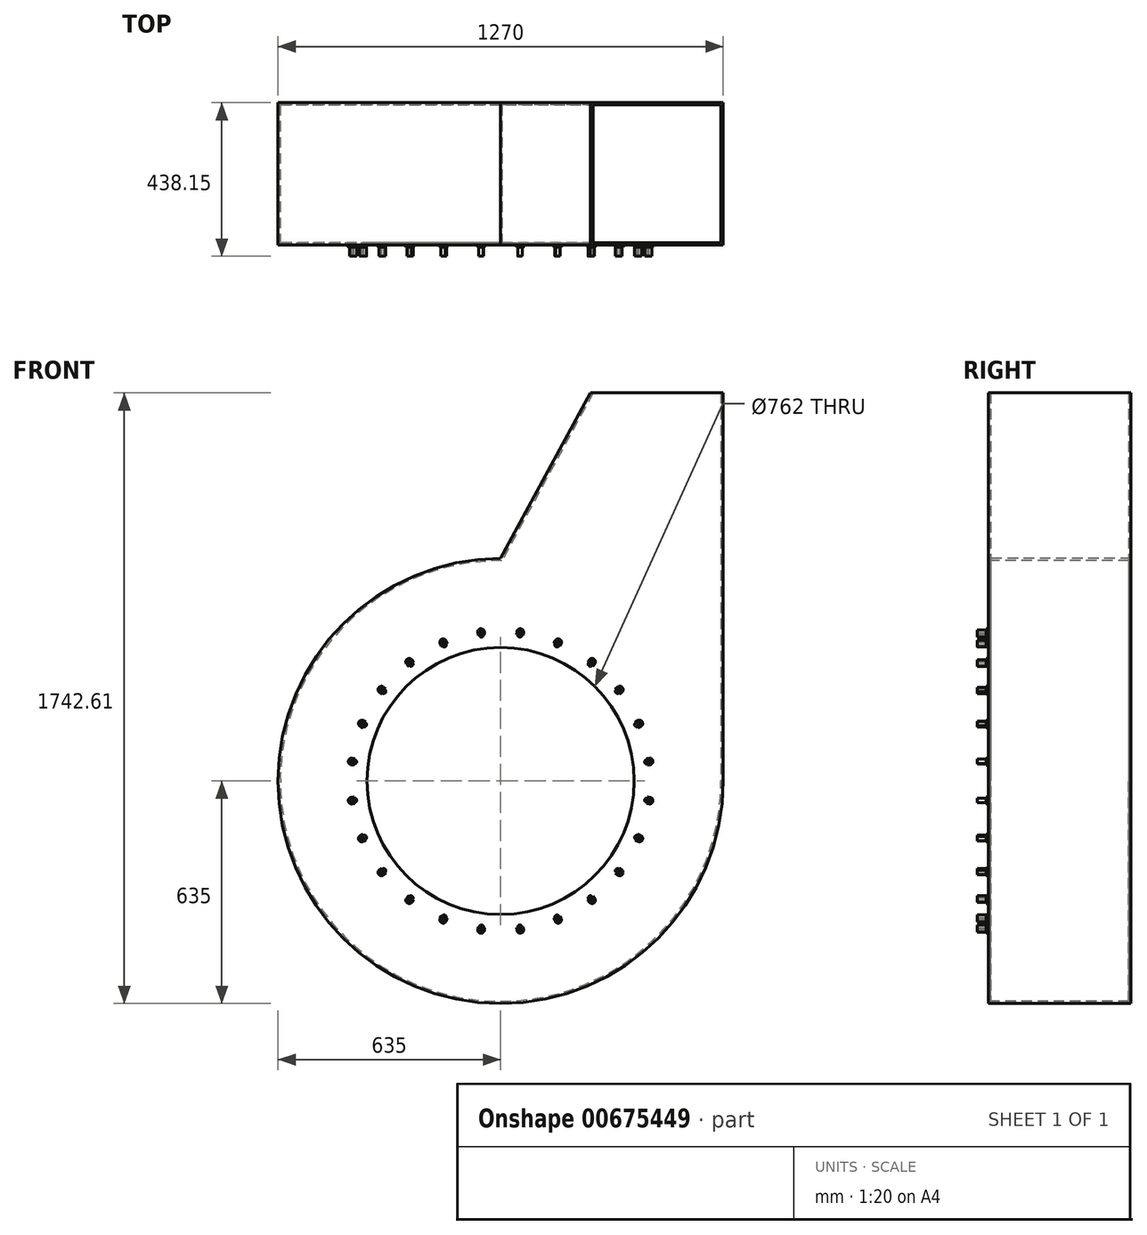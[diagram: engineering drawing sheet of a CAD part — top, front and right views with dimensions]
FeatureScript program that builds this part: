
annotation { "Feature Type Name" : "Feature", "Feature Type Description" : "" }
export const myFeature = defineFeature(function(context is Context, id is Id, definition is map)
    precondition{}
    {
        {
            var Q0;
            Q0=qCreatedBy(makeId("Front.planeOp"),FACE);
            var sketch = newSketch(context, id + "F0", { "sketchPlane" : qUnion([Q0])});
            skCircle(sketch, "E0", {"center": v(0, 0) * mm, "radius": 635 * mm});
            skLineSegment(sketch, "E1", {"start": v(635, 1107.6) * mm, "end": v(256.57, 1107.6) * mm});
            skLineSegment(sketch, "E2", {"start": v(256.57, 1107.6) * mm, "end": v(0, 635) * mm});
            skLineSegment(sketch, "E3", {"start": v(635, 1107.6) * mm, "end": v(635, 0) * mm});
            skCircle(sketch, "E4", {"center": v(0, 0) * mm, "radius": 428.63 * mm, "construction": true});
            skLineSegment(sketch, "E5", {"start": v(0, 0) * mm, "end": v(0, 611.06) * mm, "construction": true});
            skLineSegment(sketch, "E6", {"start": v(0, 0) * mm, "end": v(80.45, 611.06) * mm, "construction": true});
            skCircle(sketch, "E7", {"center": v(55.95, 424.96) * mm, "radius": 6.35 * mm});
            skCircle(sketch, "E8", {"center": v(0, 0) * mm, "radius": 381 * mm});
            skSolve(sketch);
        }
        {
            var Q0;
            Q0=qCreatedBy(makeId("Front.planeOp"),FACE);
            var sketch = newSketch(context, id + "F1", { "sketchPlane" : qUnion([Q0])});
            skCircle(sketch, "E9", {"center": v(0, 0) * mm, "radius": 420.69 * mm, "construction": true});
            skLineSegment(sketch, "E10.0", {"start": v(0, 0) * mm, "end": v(80.45, 611.06) * mm, "construction": true});
            skCircle(sketch, "E11", {"center": v(54.91, 417.09) * mm, "radius": 6.35 * mm});
            skSolve(sketch);
        }
        {
            var Q0;
            Q0=makeQuery(id+"F0.imprint","IMPRINT",FACE,{"disambiguationData":[TD([[makeQuery(id+"F0.imprint","IMPRINT",EDGE,{"derivedFrom":sQuery(id+"F0.wireOp",EDGE,"E1")}),1.0]])]});
            var Q1;
            Q1=makeQuery(id+"F0.imprint","IMPRINT",FACE,{"disambiguationData":[TD([[makeQuery(id+"F0.imprint","IMPRINT",EDGE,{"derivedFrom":sQuery(id+"F0.wireOp",EDGE,"E7")}),-1.0]])]});
            var Q2;
            Q2=makeQuery(id+"F0.imprint","IMPRINT",FACE,{"disambiguationData":[TD([[makeQuery(id+"F0.imprint","IMPRINT",EDGE,{"derivedFrom":sQuery(id+"F0.wireOp",EDGE,"E8")}),1.0]])]});
            var Q3;
            Q3=makeQuery(id+"F0.imprint","IMPRINT",FACE,{"disambiguationData":[TD([[makeQuery(id+"F0.imprint","IMPRINT",EDGE,{"derivedFrom":sQuery(id+"F0.wireOp",EDGE,"E7")}),1.0]])]});
            extrude(context, id + "F2", {"entities" : qUnion([Q0, Q1, Q2, Q3]), "oppositeDirection" : true, "depth" : 406.4 * mm, "offsetDistance" : 25.4 * mm});
        }
        {
            var Q0;
            Q0=makeQuery(id+"F2.opExtrude","SWEPT_FACE",FACE,{"disambiguationData":[OSD([sQuery(id+"F0.wireOp",EDGE,"E1")])]});
            shell(context, id + "F3", {"entities" : qUnion([Q0]), "thickness" : 6.35 * mm});
        }
        {
            var Q0;
            Q0=makeQuery(id+"F0.imprint","IMPRINT",FACE,{"disambiguationData":[TD([[makeQuery(id+"F0.imprint","IMPRINT",EDGE,{"derivedFrom":sQuery(id+"F0.wireOp",EDGE,"E8")}),1.0]])]});
            extrude(context, id + "F4", {"entities" : qUnion([Q0]), "operationType" : NewBodyOperationType.REMOVE, "endBound" : BoundingType.UP_TO_NEXT, "oppositeDirection" : true, "depth" : 25.4 * mm, "offsetDistance" : 25.4 * mm});
        }
        {
            var Q0;
            Q0=makeQuery(id+"F0.imprint","IMPRINT",FACE,{"disambiguationData":[TD([[makeQuery(id+"F0.imprint","IMPRINT",EDGE,{"derivedFrom":sQuery(id+"F0.wireOp",EDGE,"E7")}),1.0]])]});
            extrude(context, id + "F5", {"entities" : qUnion([Q0]), "depth" : 31.75 * mm, "offsetDistance" : 25.4 * mm});
        }
        {
            var Q0;
            Q0=makeQuery(id+"F5.opExtrude","SWEPT_BODY",BODY,{"disambiguationData":[OSD([sQuery(id+"F0.wireOp",EDGE,"E7")])]});
            var Q1;
            Q1=sQuery(id+"F0.wireOp",EDGE,"E4");
            circularPattern(context, id + "F6", {"entities" : qUnion([Q0]), "axis" : qUnion([Q1]), "angle" : 360 * degree, "instanceCount" : 24, "equalSpace" : true});
        }
        {
            var Q0;
            Q0=makeQuery(id+"F1.imprint","IMPRINT",FACE,{"disambiguationData":[TD([[makeQuery(id+"F1.imprint","IMPRINT",EDGE,{"derivedFrom":sQuery(id+"F1.wireOp",EDGE,"E11")}),1.0]])]});
            extrude(context, id + "F7", {"entities" : qUnion([Q0]), "depth" : 31.75 * mm, "offsetDistance" : 25.4 * mm});
        }
        {
            var Q0;
            Q0=makeQuery(id+"F7.opExtrude","SWEPT_BODY",BODY,{"disambiguationData":[OSD([sQuery(id+"F1.wireOp",EDGE,"E11")])]});
            var Q1;
            Q1=sQuery(id+"F1.wireOp",EDGE,"E9");
            circularPattern(context, id + "F8", {"entities" : qUnion([Q0]), "axis" : qUnion([Q1]), "angle" : 360 * degree, "instanceCount" : 24, "equalSpace" : true});
        }
        {
            var Q0;
            Q0=qCreatedBy(makeId("Front.planeOp"),FACE);
            var sketch = newSketch(context, id + "F9", { "sketchPlane" : qUnion([Q0])});
            skCircle(sketch, "E12.0", {"center": v(0, 0) * mm, "radius": 428.63 * mm, "construction": true});
            skCircle(sketch, "E13.0", {"center": v(0, 0) * mm, "radius": 420.69 * mm, "construction": true});
            skLineSegment(sketch, "E14.0", {"start": v(0, 0) * mm, "end": v(80.45, 611.06) * mm, "construction": true});
            skCircle(sketch, "E15", {"center": v(55.95, 424.96) * mm, "radius": 9.53 * mm});
            skCircle(sketch, "E16", {"center": v(54.91, 417.09) * mm, "radius": 9.53 * mm});
            skLineSegment(sketch, "E17", {"start": v(65.4, 423.71) * mm, "end": v(64.35, 415.85) * mm});
            skLineSegment(sketch, "E18", {"start": v(46.5, 426.2) * mm, "end": v(45.47, 418.33) * mm});
            skSolve(sketch);
        }
        {
            var Q0;
            {var subQ0=sQuery(id+"F9.wireOp",EDGE,"E15");var subQ1=makeQuery(id+"F9.imprint","INTERSECT",VERTEX,{"derivedFrom":[subQ0,sQuery(id+"F9.wireOp",EDGE,"E18")]});Q0=makeQuery(id+"F9.imprint","IMPRINT",FACE,{"disambiguationData":[TD([[makeQuery(id+"F9.imprint","IMPRINT",EDGE,{"disambiguationData":[TD([[subQ1,-1.0]])],"derivedFrom":subQ0}),1.0]])]});}
            var Q1;
            {var subQ0=sQuery(id+"F9.wireOp",EDGE,"E16");var subQ1=sQuery(id+"F9.wireOp",EDGE,"E15");var subQ2=makeQuery(id+"F9.imprint","INTERSECT",VERTEX,{"disambiguationData":[OD(0.0)],"derivedFrom":[subQ1,subQ0]});Q1=makeQuery(id+"F9.imprint","IMPRINT",FACE,{"disambiguationData":[TD([[makeQuery(id+"F9.imprint","IMPRINT",EDGE,{"disambiguationData":[TD([[subQ2,-1.0]])],"derivedFrom":subQ1}),1.0]])]});}
            var Q2;
            {var subQ0=sQuery(id+"F9.wireOp",EDGE,"E16");var subQ1=sQuery(id+"F9.wireOp",EDGE,"E15");var subQ2=makeQuery(id+"F9.imprint","INTERSECT",VERTEX,{"disambiguationData":[OD(0.0)],"derivedFrom":[subQ1,subQ0]});Q2=makeQuery(id+"F9.imprint","IMPRINT",FACE,{"disambiguationData":[TD([[makeQuery(id+"F9.imprint","IMPRINT",EDGE,{"disambiguationData":[TD([[subQ2,-1.0]])],"derivedFrom":subQ1}),-1.0]])]});}
            var Q3;
            {var subQ0=sQuery(id+"F9.wireOp",EDGE,"E18");Q3=makeQuery(id+"F9.imprint","IMPRINT",FACE,{"disambiguationData":[TD([[makeQuery(id+"F9.imprint","IMPRINT",EDGE,{"derivedFrom":subQ0}),1.0]])]});}
            var Q4;
            {var subQ0=sQuery(id+"F9.wireOp",EDGE,"E17");Q4=makeQuery(id+"F9.imprint","IMPRINT",FACE,{"disambiguationData":[TD([[makeQuery(id+"F9.imprint","IMPRINT",EDGE,{"derivedFrom":subQ0}),-1.0]])]});}
            extrude(context, id + "F10", {"entities" : qUnion([Q0, Q1, Q2, Q3, Q4]), "depth" : 6.35 * mm, "offsetDistance" : 25.4 * mm});
        }
        {
            var Q0;
            Q0=makeQuery(id+"F10.opExtrude","SWEPT_BODY",BODY,{"disambiguationData":[OSD([sQuery(id+"F9.wireOp",EDGE,"E15"),sQuery(id+"F9.wireOp",EDGE,"E16"),sQuery(id+"F9.wireOp",EDGE,"E17"),sQuery(id+"F9.wireOp",EDGE,"E18")])]});
            var Q1;
            Q1=sQuery(id+"F1.wireOp",EDGE,"E9");
            circularPattern(context, id + "F11", {"entities" : qUnion([Q0]), "axis" : qUnion([Q1]), "angle" : 360 * degree, "instanceCount" : 24, "equalSpace" : true});
        }
    });
